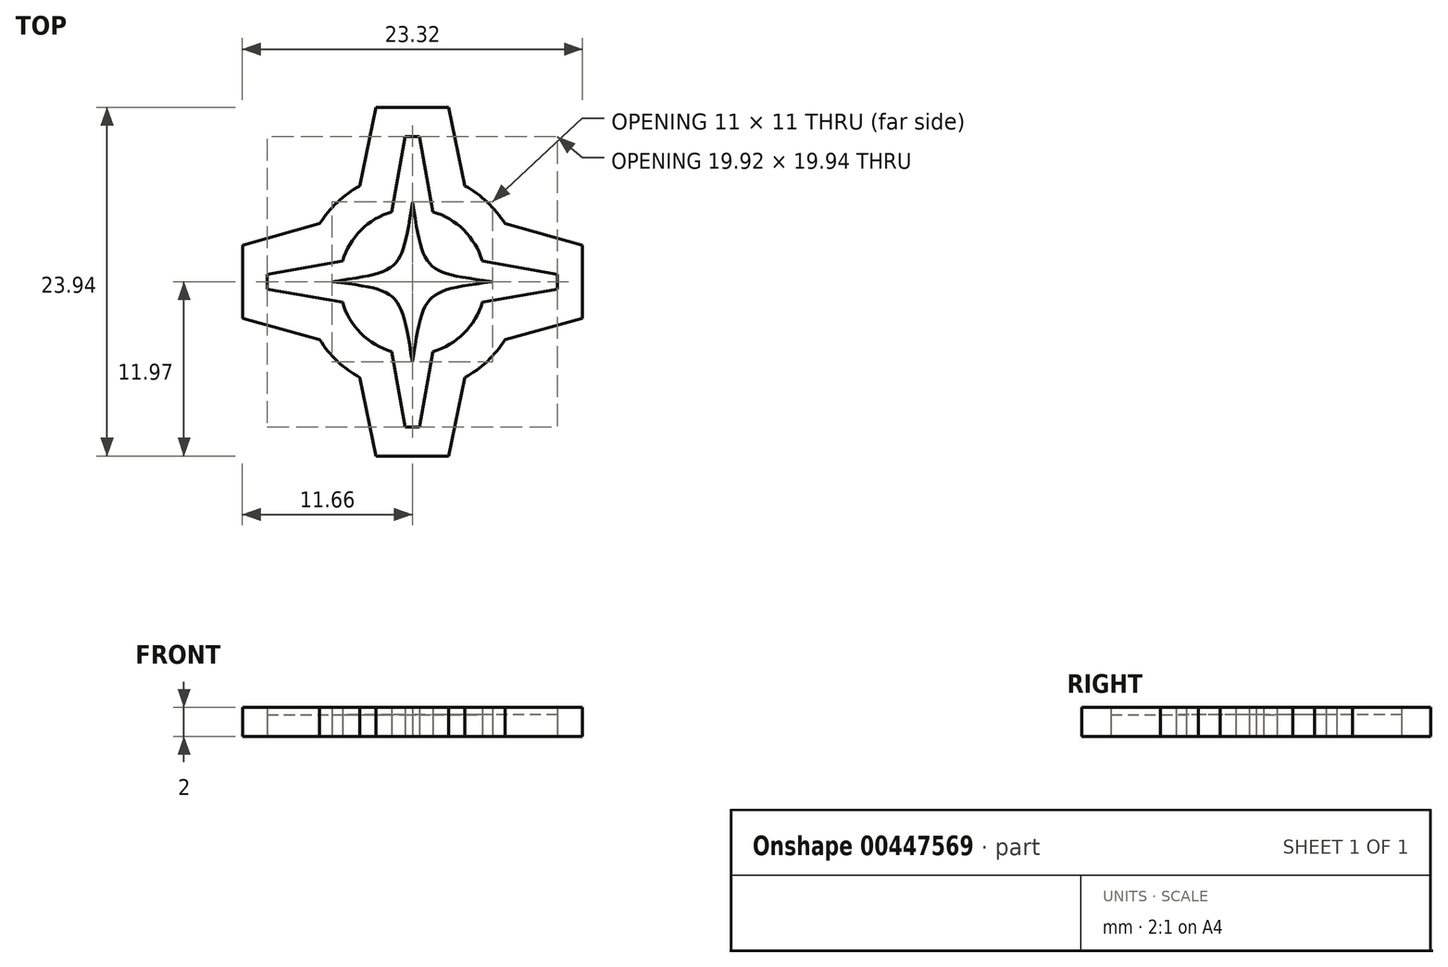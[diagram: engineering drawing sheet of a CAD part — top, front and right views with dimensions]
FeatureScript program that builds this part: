
annotation { "Feature Type Name" : "Feature", "Feature Type Description" : "" }
export const myFeature = defineFeature(function(context is Context, id is Id, definition is map)
    precondition{}
    {
        {
            var Q0;
            Q0=qCreatedBy(makeId("Top.planeOp"),FACE);
            var sketch = newSketch(context, id + "F0", { "sketchPlane" : qUnion([Q0])});
            skLineSegment(sketch, "E0", {"start": v(-2.5, 11.97) * mm, "end": v(2.5, 11.97) * mm});
            skLineSegment(sketch, "E1", {"start": v(-2.5, 11.97) * mm, "end": v(-3.6, 6.58) * mm});
            skLineSegment(sketch, "E2", {"start": v(2.5, 11.97) * mm, "end": v(3.6, 6.58) * mm});
            skLineSegment(sketch, "E3.MirrorCS", {"start": v(-2.5, -11.97) * mm, "end": v(-3.6, -6.58) * mm});
            skLineSegment(sketch, "E4.MirrorCS", {"start": v(-2.5, -11.97) * mm, "end": v(2.5, -11.97) * mm});
            skLineSegment(sketch, "E5.MirrorCS", {"start": v(2.5, -11.97) * mm, "end": v(3.6, -6.58) * mm});
            skLineSegment(sketch, "E6", {"start": v(11.66, 2.5) * mm, "end": v(11.66, -2.5) * mm});
            skLineSegment(sketch, "E7", {"start": v(11.66, -2.5) * mm, "end": v(6.36, -3.98) * mm});
            skLineSegment(sketch, "E8", {"start": v(11.66, 2.5) * mm, "end": v(6.36, 3.98) * mm});
            skLineSegment(sketch, "E9.MirrorCS", {"start": v(-11.66, 2.5) * mm, "end": v(-6.36, 3.98) * mm});
            skLineSegment(sketch, "E10.MirrorCS", {"start": v(-11.66, 2.5) * mm, "end": v(-11.66, -2.5) * mm});
            skLineSegment(sketch, "E11.MirrorCS", {"start": v(-11.66, -2.5) * mm, "end": v(-6.36, -3.98) * mm});
            skArc(sketch, "E12", {"start": v(-3.6, 6.58) * mm, "mid": v(-5.15, 5.46) * mm, "end": v(-6.36, 3.98) * mm});
            skArc(sketch, "E13.trimOffspring", {"start": v(-6.36, -3.98) * mm, "mid": v(-5.15, -5.46) * mm, "end": v(-3.6, -6.58) * mm});
            skArc(sketch, "E14.trimOffspring", {"start": v(6.36, 3.98) * mm, "mid": v(5.15, 5.46) * mm, "end": v(3.6, 6.58) * mm});
            skArc(sketch, "E15.trimOffspring", {"start": v(3.6, -6.58) * mm, "mid": v(5.15, -5.46) * mm, "end": v(6.36, -3.98) * mm});
            skArc(sketch, "E16", {"start": v(-1.4, 4.8) * mm, "mid": v(-3.53, 3.54) * mm, "end": v(-4.8, 1.43) * mm});
            skLineSegment(sketch, "E17", {"start": v(-0.5, 9.97) * mm, "end": v(0.5, 9.97) * mm});
            skLineSegment(sketch, "E18", {"start": v(0.5, 9.97) * mm, "end": v(1.4, 4.8) * mm});
            skLineSegment(sketch, "E19", {"start": v(-0.5, 9.97) * mm, "end": v(-1.4, 4.8) * mm});
            skLineSegment(sketch, "E20", {"start": v(9.96, 0.5) * mm, "end": v(9.96, -0.5) * mm});
            skLineSegment(sketch, "E21", {"start": v(9.96, -0.5) * mm, "end": v(4.79, -1.4) * mm});
            skLineSegment(sketch, "E22", {"start": v(9.96, 0.5) * mm, "end": v(4.8, 1.43) * mm});
            skLineSegment(sketch, "E23.MirrorCS", {"start": v(-9.96, 0.5) * mm, "end": v(-4.8, 1.43) * mm});
            skLineSegment(sketch, "E24.MirrorCS", {"start": v(-9.96, 0.5) * mm, "end": v(-9.96, -0.5) * mm});
            skLineSegment(sketch, "E25.MirrorCS", {"start": v(-9.96, -0.5) * mm, "end": v(-4.79, -1.4) * mm});
            skLineSegment(sketch, "E26.MirrorCS", {"start": v(-0.5, -9.97) * mm, "end": v(-1.4, -4.8) * mm});
            skLineSegment(sketch, "E27.MirrorCS", {"start": v(-0.5, -9.97) * mm, "end": v(0.5, -9.97) * mm});
            skLineSegment(sketch, "E28.MirrorCS", {"start": v(0.5, -9.97) * mm, "end": v(1.4, -4.8) * mm});
            skArc(sketch, "E29.trimOffspring", {"start": v(-4.8, -1.4) * mm, "mid": v(-3.54, -3.53) * mm, "end": v(-1.4, -4.8) * mm});
            skArc(sketch, "E30.trimOffspring", {"start": v(4.8, 1.43) * mm, "mid": v(3.53, 3.54) * mm, "end": v(1.4, 4.8) * mm});
            skArc(sketch, "E31.trimOffspring", {"start": v(1.4, -4.8) * mm, "mid": v(3.54, -3.53) * mm, "end": v(4.8, -1.4) * mm});
            skFitSpline(sketch, "E32", {"points": [v(-5.5, 0) * mm, v(0, -5.5) * mm], "startDerivative": vector(14.06, -1.75) * mm, "endDerivative": vector(2.44, -14.75) * mm});
            skFitSpline(sketch, "E33", {"points": [v(0, -5.5) * mm, v(5.5, 0) * mm], "startDerivative": vector(2.3, 14.58) * mm, "endDerivative": vector(14.2, 1.92) * mm});
            skFitSpline(sketch, "E34", {"points": [v(5.5, 0) * mm, v(0, 5.5) * mm], "startDerivative": vector(-14.2, 1.93) * mm, "endDerivative": vector(-2.3, 14.57) * mm});
            skFitSpline(sketch, "E35", {"points": [v(0, 5.5) * mm, v(-5.5, 0) * mm], "startDerivative": vector(-2.17, -14.43) * mm, "endDerivative": vector(-14.33, -2.07) * mm});
            skSolve(sketch);
        }
        {
            var Q0;
            Q0=makeQuery(id+"F0.imprint","IMPRINT",FACE,{"disambiguationData":[TD([[makeQuery(id+"F0.imprint","IMPRINT",EDGE,{"derivedFrom":sQuery(id+"F0.wireOp",EDGE,"E0")}),-1.0]])]});
            var Q1;
            Q1=makeQuery(id+"F0.imprint","IMPRINT",FACE,{"disambiguationData":[TD([[makeQuery(id+"F0.imprint","IMPRINT",EDGE,{"derivedFrom":sQuery(id+"F0.wireOp",EDGE,"E32")}),1.0]])]});
            extrude(context, id + "F1", {"entities" : qUnion([Q0, Q1]), "depth" : 2 * mm});
        }
        {
            var Q0;
            Q0=makeQuery(id+"F0.imprint","IMPRINT",FACE,{"disambiguationData":[TD([[makeQuery(id+"F0.imprint","IMPRINT",EDGE,{"derivedFrom":sQuery(id+"F0.wireOp",EDGE,"E16")}),1.0]])]});
            extrude(context, id + "F2", {"entities" : qUnion([Q0]), "depth" : 1.5 * mm});
        }
    });
